# Revit family: TOPWET_Střešní vpust TW(E) 125 V
name_source: partatom
category: Instalační zařizovací předměty
revit_build: Autodesk Revit 2016 (Build: 20151007_0715(x64)
units: mm (PartAtom-declared; Revit-internal decimal feet)

## family parameters
Bod výpočtu místnosti = Ne
Kóta kulaté spojky = Použít průměr
Nadpis OmniClass = Waste Water Drains
Ořezat dutým tvarem při načtení = Ne
Sdílené = Ne
Typ součásti = Normální
Vždy vertikální = Ano
Založené na pracovní rovině = Ano
Číslo OmniClass = 23.70.50.21.24

## types (6) — shared parameters
JMENOVITÝ PRŮMĚR = 125 mm
Model = viz OBJEDNACÍ KÓD
PRŮTOK = 8.5 L/s
Popis = Vpusť
Připojení odpadu = Ano
URL = http://www.topwet.cz
Výrobce = TOPWET
zero-valued in all types: Cena, Výchozí výška

## per-type parameters (varying)
| type | EV | Klíčová poznámka | Komentáře k typům | Límec_Materiál | T | Typ obrázku |
| TW 125 BIT V vodorovné provedení, manžeta z asfaltového pásu | Ne | TW 125 BIT V | Střešní vpust TOPWET s integrovanou manžetou  z modifikovaného asfaltového pásu, vodorovné provedení s ochranným košem | Plast - černý | 1 | tw-bit-v.png |
| TW 125 PVC V vodorovné provedení, manžeta z PVC | Ne | TW 125 PVC V | Střešní vpust TOPWET s integrovanou manžetou z hydroizolační fólie na bázi PVC, vodorovné provedení s ochranným košem | Plast - hnědý | 2 | tw-pvc-v.png |
| TW 125___V vodorovné provedení, manžeta na zakázku | Ne | TW 125 ___ V | Střešní vpust TOPWET s integrovanou manžetou na zakázku (EPDM, TPO, FPO, STE, PE), vodorovné provedení s ochranným košem | Plast - šedý | 3 | tw-epdm-v.png |
| TWE 125___V vodorovné provedení, manžeta na zakázku, vyhřívaná | Ano | TWE 125 ___ V | Střešní vpust TOPWET s integrovanou manžetou na zakázku (EPDM, TPO, FPO, STE, PE), vodorovné provedení s ochranným košem, vyhřívaná 230 V s připojovacím kabelem | Plast - šedý | 3 | twe-epdm-v.png |
| TWE 125 BIT V vodorovné provedení, manžeta z asfaltového pásu, vyhřívaná | Ano | TWE 125 BIT V | Střešní vpust TOPWET s integrovanou manžetou z modifikovaného asfaltového pásu, vodorovné provedení s ochranným košem, vyhřívaná 230 V s připojovacím kabelem | Plast - černý | 1 | twe-bit-v.png |
| TWE 125 PVC V vodorvné provedení, manžeta z PVC, vyhřívaná | Ano | TWE 125 PVC V | Střešní vpust TOPWET s integrovanou manžetou z hydroizolační fólie na bázi PVC, vodorovné provedení s ochranným košem, vyhřívaná 230 V s připojovacím kabelem | Plast - hnědý | 2 | twe-pvc-v.png |
